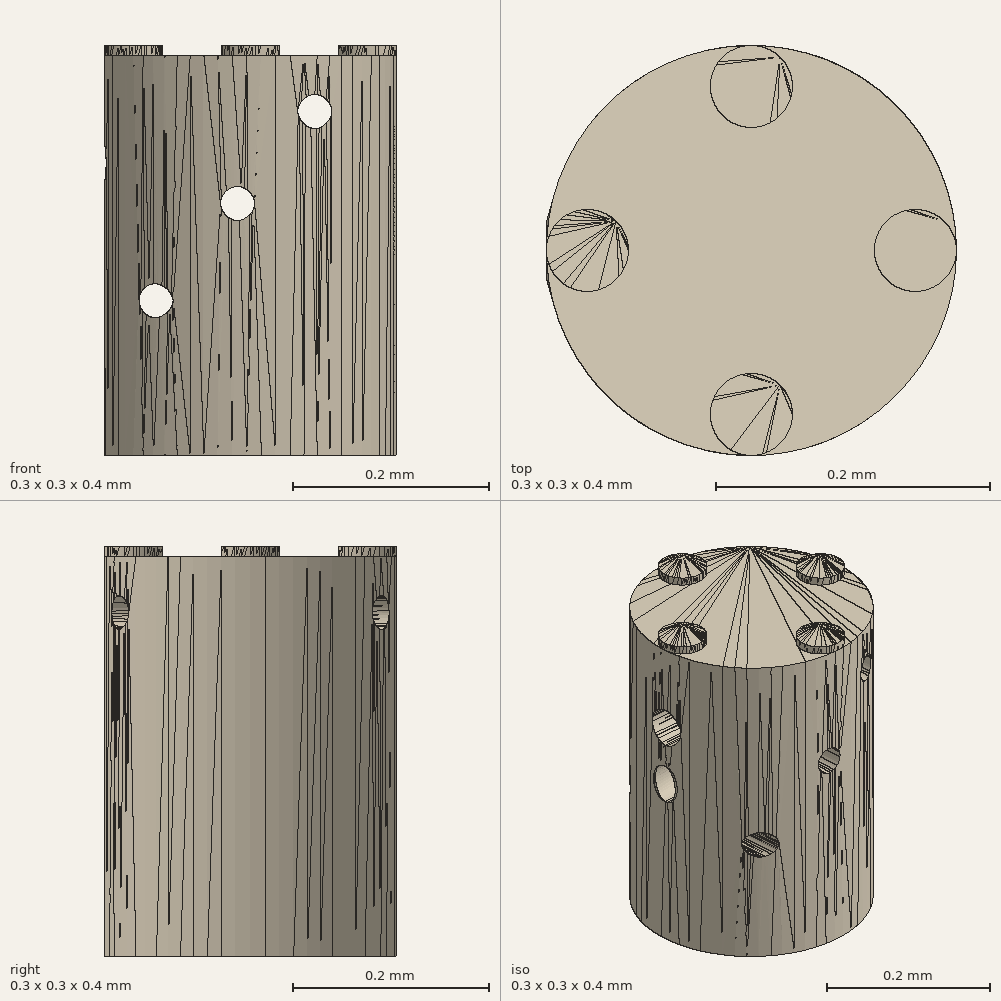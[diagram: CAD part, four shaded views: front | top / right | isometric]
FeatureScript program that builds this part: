
annotation { "Feature Type Name" : "Feature", "Feature Type Description" : "" }
export const myFeature = defineFeature(function(context is Context, id is Id, definition is map)
    precondition{}
    {
        {
            var Q0;
            Q0=qCreatedBy(makeId("Top.planeOp"),FACE);
            var sketch = newSketch(context, id + "F0", { "sketchPlane" : qUnion([Q0])});
            skCircle(sketch, "E0", {"center": v(0, 0) * mm, "radius": 0.15 * mm});
            skSolve(sketch);
        }
        {
            var Q0;
            Q0 = qSketchRegion(id + "F0", true);
            extrude(context, id + "F1", {"entities" : qUnion([Q0]), "depth" : 0.4 * mm, "offsetDistance" : 25 * mm});
        }
        {
            var Q0;
            Q0=qCreatedBy(makeId("Top.planeOp"),FACE);
            var sketch = newSketch(context, id + "F2", { "sketchPlane" : qUnion([Q0])});
            skCircle(sketch, "E1", {"center": v(0, 0) * mm, "radius": 0.07 * mm});
            skSolve(sketch);
        }
        {
            var Q0;
            Q0 = qSketchRegion(id + "F2", true);
            extrude(context, id + "F3", {"entities" : qUnion([Q0]), "operationType" : NewBodyOperationType.REMOVE, "depth" : 0.12 * mm, "offsetDistance" : 25 * mm});
        }
        {
            var Q0;
            Q0=qCreatedBy(makeId("Front.planeOp"),FACE);
            var sketch = newSketch(context, id + "F4", { "sketchPlane" : qUnion([Q0])});
            skLineSegment(sketch, "E2", {"start": v(0.06, 0.38) * mm, "end": v(-0.12, 0.15) * mm});
            skLineSegment(sketch, "E3", {"start": v(-0.12, 0.15) * mm, "end": v(-0.1, 0.13) * mm});
            skLineSegment(sketch, "E4", {"start": v(-0.1, 0.13) * mm, "end": v(0.1, 0.36) * mm});
            skLineSegment(sketch, "E5", {"start": v(0.1, 0.36) * mm, "end": v(0.06, 0.38) * mm});
            skSolve(sketch);
        }
        {
            var Q0;
            Q0 = qSketchRegion(id + "F4", true);
            extrude(context, id + "F5", {"entities" : qUnion([Q0]), "operationType" : NewBodyOperationType.REMOVE, "oppositeDirection" : true, "depth" : 0.05 * mm, "offsetDistance" : 25 * mm});
        }
        {
            var Q0;
            Q0 = qSketchRegion(id + "F4", true);
            extrude(context, id + "F6", {"entities" : qUnion([Q0]), "operationType" : NewBodyOperationType.REMOVE, "depth" : 0.05 * mm, "offsetDistance" : 25 * mm});
        }
        {
            var Q0;
            Q0=qCreatedBy(makeId("Front.planeOp"),FACE);
            var sketch = newSketch(context, id + "F7", { "sketchPlane" : qUnion([Q0])});
            skCircle(sketch, "E6", {"center": v(-0.1, 0.16) * mm, "radius": 0.02 * mm});
            skCircle(sketch, "E7", {"center": v(0.07, 0.35) * mm, "radius": 0.02 * mm});
            skCircle(sketch, "E8", {"center": v(-0.01, 0.26) * mm, "radius": 0.02 * mm});
            skSolve(sketch);
        }
        {
            var Q0;
            Q0 = qSketchRegion(id + "F7", true);
            extrude(context, id + "F8", {"entities" : qUnion([Q0]), "operationType" : NewBodyOperationType.REMOVE, "oppositeDirection" : true, "depth" : 1 * mm, "offsetDistance" : 25 * mm});
        }
        {
            var Q0;
            Q0 = qSketchRegion(id + "F7", true);
            extrude(context, id + "F9", {"entities" : qUnion([Q0]), "operationType" : NewBodyOperationType.REMOVE, "depth" : 1 * mm, "offsetDistance" : 25 * mm});
        }
        {
            var Q0;
            Q0=qCreatedBy(makeId("Right.planeOp"),FACE);
            var sketch = newSketch(context, id + "F10", { "sketchPlane" : qUnion([Q0])});
            skCircle(sketch, "E9", {"center": v(0, 0.3) * mm, "radius": 0.03 * mm});
            skSolve(sketch);
        }
        {
            var Q0;
            Q0 = qSketchRegion(id + "F10", true);
            extrude(context, id + "F11", {"entities" : qUnion([Q0]), "operationType" : NewBodyOperationType.REMOVE, "oppositeDirection" : true, "depth" : 1 * mm, "offsetDistance" : 25 * mm});
        }
        {
            var Q0;
            Q0 = qSketchRegion(id + "F10", true);
            extrude(context, id + "F12", {"entities" : qUnion([Q0]), "operationType" : NewBodyOperationType.REMOVE, "depth" : 0.01 * mm, "offsetDistance" : 25 * mm});
        }
        {
            var Q0;
            Q0=qCreatedBy(makeId("Right.planeOp"),FACE);
            cPlane(context, id + "F13", {"entities" : qUnion([Q0]), "cplaneType" : CPlaneType.OFFSET, "offset" : 0.15 * mm, "oppositeDirection" : true, "width" : 150 * mm, "height" : 150 * mm});
        }
        {
            var Q0;
            Q0=qCreatedBy(makeId("Front.planeOp"),FACE);
            var sketch = newSketch(context, id + "F14", { "sketchPlane" : qUnion([Q0])});
            skLineSegment(sketch, "E10", {"start": v(0.13, 0.43) * mm, "end": v(-0.15, 0.1) * mm});
            skSolve(sketch);
        }
        {
            var Q0;
            Q0=qCreatedBy(id+"F13.planeOp",FACE);
            var sketch = newSketch(context, id + "F15", { "sketchPlane" : qUnion([Q0])});
            skCircle(sketch, "E11", {"center": v(0, 0.22) * mm, "radius": 0.03 * mm});
            skSolve(sketch);
        }
        {
            var Q0;
            Q0 = qSketchRegion(id + "F15", true);
            extrude(context, id + "F16", {"entities" : qUnion([Q0]), "operationType" : NewBodyOperationType.REMOVE, "depth" : 0.1 * mm, "offsetDistance" : 25 * mm});
        }
        {
            var Q0;
            Q0=qCreatedBy(makeId("Top.planeOp"),FACE);
            cPlane(context, id + "F17", {"entities" : qUnion([Q0]), "cplaneType" : CPlaneType.OFFSET, "offset" : 0.4 * mm, "width" : 150 * mm, "height" : 150 * mm});
        }
        {
            var Q0;
            Q0=qCreatedBy(id+"F17.planeOp",FACE);
            var sketch = newSketch(context, id + "F18", { "sketchPlane" : qUnion([Q0])});
            skCircle(sketch, "E12", {"center": v(0, 0.12) * mm, "radius": 0.03 * mm});
            skCircle(sketch, "E13", {"center": v(-0.12, 0) * mm, "radius": 0.03 * mm});
            skCircle(sketch, "E14", {"center": v(0, -0.12) * mm, "radius": 0.03 * mm});
            skCircle(sketch, "E15", {"center": v(0.12, 0) * mm, "radius": 0.03 * mm});
            skSolve(sketch);
        }
        {
            var Q0;
            Q0 = qSketchRegion(id + "F18", true);
            extrude(context, id + "F19", {"entities" : qUnion([Q0]), "depth" : 0.01 * mm, "offsetDistance" : 25 * mm});
        }
    });
